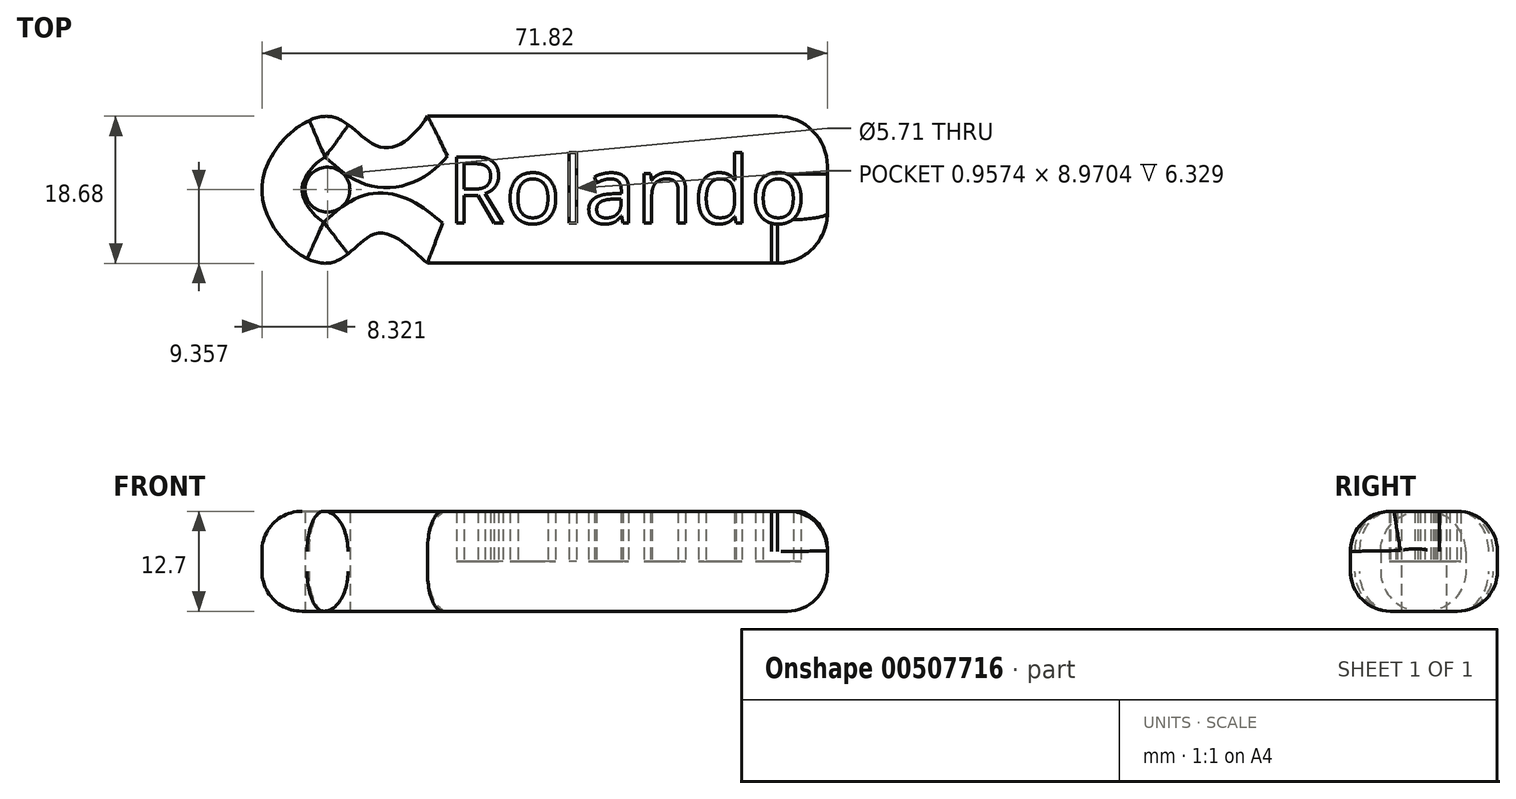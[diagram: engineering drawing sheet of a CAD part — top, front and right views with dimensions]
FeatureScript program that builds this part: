
annotation { "Feature Type Name" : "Feature", "Feature Type Description" : "" }
export const myFeature = defineFeature(function(context is Context, id is Id, definition is map)
    precondition{}
    {
        {
            var Q0;
            Q0=qCreatedBy(makeId("Top.planeOp"),FACE);
            var sketch = newSketch(context, id + "F0", { "sketchPlane" : qUnion([Q0])});
            skLineSegment(sketch, "E0.bottom", {"start": v(-23.1, 21.84) * mm, "end": v(21.35, 21.84) * mm});
            skLineSegment(sketch, "E0.top", {"start": v(-23.1, 3.17) * mm, "end": v(21.35, 3.17) * mm});
            skLineSegment(sketch, "E0.left", {"start": v(-23.1, 21.84) * mm, "end": v(-23.1, 3.17) * mm});
            skLineSegment(sketch, "E0.right", {"start": v(27.7, 15.49) * mm, "end": v(27.7, 9.52) * mm});
            skText(sketch, "E1", { "text": "Rolando", "fontName": "OpenSans-Regular.ttf"});
            skFitSpline(sketch, "E2", {"points": [v(-23.1, 3.17) * mm, v(-29.45, 6.98) * mm, v(-35.8, 3.17) * mm, v(-44.12, 12.52) * mm, v(-35.8, 21.84) * mm, v(-29.45, 18.03) * mm, v(-23.1, 21.84) * mm], "startDerivative": vector(-38.6, 33.31) * mm, "endDerivative": vector(39.06, 62.1) * mm});
            skCircle(sketch, "E3", {"center": v(-35.8, 12.52) * mm, "radius": 2.86 * mm});
            skPoint(sketch, "E4.visualSharp", {"position": v(27.7, 21.84) * mm});
            skArc(sketch, "E4.filletArc", {"start": v(27.7, 15.49) * mm, "mid": v(25.84, 19.98) * mm, "end": v(21.35, 21.84) * mm});
            skPoint(sketch, "E5.visualSharp", {"position": v(27.7, 3.17) * mm});
            skArc(sketch, "E5.filletArc", {"start": v(21.35, 3.17) * mm, "mid": v(25.84, 5.03) * mm, "end": v(27.7, 9.52) * mm});
            const initialGuessF0  = {"E1": [-0.02056, 0.00825, 1, 0, 0.0085]};
            skSetInitialGuess(sketch, initialGuessF0);
            skSolve(sketch);
        }
        {
            var Q0;
            Q0=makeQuery(id+"F0.imprint","IMPRINT",FACE,{"disambiguationData":[TD([[makeQuery(id+"F0.imprint","IMPRINT",EDGE,{"derivedFrom":sQuery(id+"F0.wireOp",EDGE,"E1.sketch_text.stroke-0")}),-1.0]])]});
            var Q1;
            Q1=makeQuery(id+"F0.imprint","IMPRINT",FACE,{"disambiguationData":[TD([[makeQuery(id+"F0.imprint","IMPRINT",EDGE,{"derivedFrom":sQuery(id+"F0.wireOp",EDGE,"E1.sketch_text.stroke-18")}),-1.0]])]});
            var Q2;
            Q2=makeQuery(id+"F0.imprint","IMPRINT",FACE,{"disambiguationData":[TD([[makeQuery(id+"F0.imprint","IMPRINT",EDGE,{"derivedFrom":sQuery(id+"F0.wireOp",EDGE,"E1.sketch_text.stroke-35")}),-1.0]])]});
            var Q3;
            Q3=makeQuery(id+"F0.imprint","IMPRINT",FACE,{"disambiguationData":[TD([[makeQuery(id+"F0.imprint","IMPRINT",EDGE,{"derivedFrom":sQuery(id+"F0.wireOp",EDGE,"E1.sketch_text.stroke-39")}),-1.0]])]});
            var Q4;
            Q4=makeQuery(id+"F0.imprint","IMPRINT",FACE,{"disambiguationData":[TD([[makeQuery(id+"F0.imprint","IMPRINT",EDGE,{"derivedFrom":sQuery(id+"F0.wireOp",EDGE,"E1.sketch_text.stroke-66")}),-1.0]])]});
            var Q5;
            Q5=makeQuery(id+"F0.imprint","IMPRINT",FACE,{"disambiguationData":[TD([[makeQuery(id+"F0.imprint","IMPRINT",EDGE,{"derivedFrom":sQuery(id+"F0.wireOp",EDGE,"E1.sketch_text.stroke-83")}),-1.0]])]});
            var Q6;
            Q6=makeQuery(id+"F0.imprint","IMPRINT",FACE,{"disambiguationData":[TD([[makeQuery(id+"F0.imprint","IMPRINT",EDGE,{"derivedFrom":sQuery(id+"F0.wireOp",EDGE,"E1.sketch_text.stroke-107")}),-1.0]])]});
            extrude(context, id + "F1", {"entities" : qUnion([Q0, Q1, Q2, Q3, Q4, Q5, Q6]), "depth" : 6.35 * mm});
        }
        {
            var Q0;
            Q0=makeQuery(id+"F0.imprint","IMPRINT",FACE,{"disambiguationData":[TD([[makeQuery(id+"F0.imprint","IMPRINT",EDGE,{"derivedFrom":sQuery(id+"F0.wireOp",EDGE,"E0.bottom")}),-1.0]])]});
            var Q1;
            Q1=makeQuery(id+"F0.imprint","IMPRINT",FACE,{"disambiguationData":[TD([[makeQuery(id+"F0.imprint","IMPRINT",EDGE,{"derivedFrom":sQuery(id+"F0.wireOp",EDGE,"E1.sketch_text.stroke-116")}),1.0]])]});
            var Q2;
            Q2=makeQuery(id+"F0.imprint","IMPRINT",FACE,{"disambiguationData":[TD([[makeQuery(id+"F0.imprint","IMPRINT",EDGE,{"derivedFrom":sQuery(id+"F0.wireOp",EDGE,"E1.sketch_text.stroke-98")}),1.0]])]});
            var Q3;
            Q3=makeQuery(id+"F0.imprint","IMPRINT",FACE,{"disambiguationData":[TD([[makeQuery(id+"F0.imprint","IMPRINT",EDGE,{"derivedFrom":sQuery(id+"F0.wireOp",EDGE,"E1.sketch_text.stroke-58")}),1.0]])]});
            var Q4;
            Q4=makeQuery(id+"F0.imprint","IMPRINT",FACE,{"disambiguationData":[TD([[makeQuery(id+"F0.imprint","IMPRINT",EDGE,{"derivedFrom":sQuery(id+"F0.wireOp",EDGE,"E1.sketch_text.stroke-27")}),1.0]])]});
            var Q5;
            Q5=makeQuery(id+"F0.imprint","IMPRINT",FACE,{"disambiguationData":[TD([[makeQuery(id+"F0.imprint","IMPRINT",EDGE,{"derivedFrom":sQuery(id+"F0.wireOp",EDGE,"E1.sketch_text.stroke-11")}),1.0]])]});
            extrude(context, id + "F2", {"entities" : qUnion([Q0, Q1, Q2, Q3, Q4, Q5]), "operationType" : NewBodyOperationType.ADD, "depth" : 12.7 * mm});
        }
        {
            var Q0;
            Q0 = qSketchRegion(id + "F0", true);
            extrude(context, id + "F3", {"entities" : qUnion([Q0]), "operationType" : NewBodyOperationType.ADD, "depth" : 12.7 * mm});
        }
        {
            var Q0;
            Q0=makeQuery(id+"F2.opExtrude","SWEPT_EDGE",EDGE,{"disambiguationData":[OSD([sQuery(id+"F0.wireOp",EDGE,"E0.right"),sQuery(id+"F0.wireOp",EDGE,"E4.filletArc")])]});
            var Q1;
            Q1=makeQuery(id+"F2.opExtrude","SWEPT_EDGE",EDGE,{"disambiguationData":[OSD([sQuery(id+"F0.wireOp",EDGE,"E0.right"),sQuery(id+"F0.wireOp",EDGE,"E5.filletArc")])]});
            var Q2;
            Q2=makeQuery(id+"F2.opExtrude","CAP_EDGE",EDGE,{"disambiguationData":[OSD([sQuery(id+"F0.wireOp",EDGE,"E0.right")])],"isStart":true});
            var Q3;
            Q3=makeQuery(id+"F2.opExtrude","CAP_EDGE",EDGE,{"disambiguationData":[OSD([sQuery(id+"F0.wireOp",EDGE,"E5.filletArc")])],"isStart":true});
            var Q4;
            Q4=makeQuery(id+"F2.opExtrude","CAP_EDGE",EDGE,{"disambiguationData":[OSD([sQuery(id+"F0.wireOp",EDGE,"E0.bottom")])],"isStart":true});
            var Q5;
            Q5=makeQuery(id+"F2.opExtrude","CAP_EDGE",EDGE,{"disambiguationData":[OSD([sQuery(id+"F0.wireOp",EDGE,"E0.bottom")])],"isStart":false});
            var Q6;
            Q6=makeQuery(id+"F3.opExtrude","CAP_EDGE",EDGE,{"disambiguationData":[OSD([sQuery(id+"F0.wireOp",EDGE,"E2")])],"isStart":true});
            var Q7;
            Q7=makeQuery(id+"F3.opExtrude","CAP_EDGE",EDGE,{"disambiguationData":[OSD([sQuery(id+"F0.wireOp",EDGE,"E2")])],"isStart":false});
            fillet(context, id + "F4", {"entities" : qUnion([Q0, Q1, Q2, Q3, Q4, Q5, Q6, Q7]), "radius" : 5.08 * mm, "tangentPropagation" : true, "allowEdgeOverflow" : false});
        }
    });
